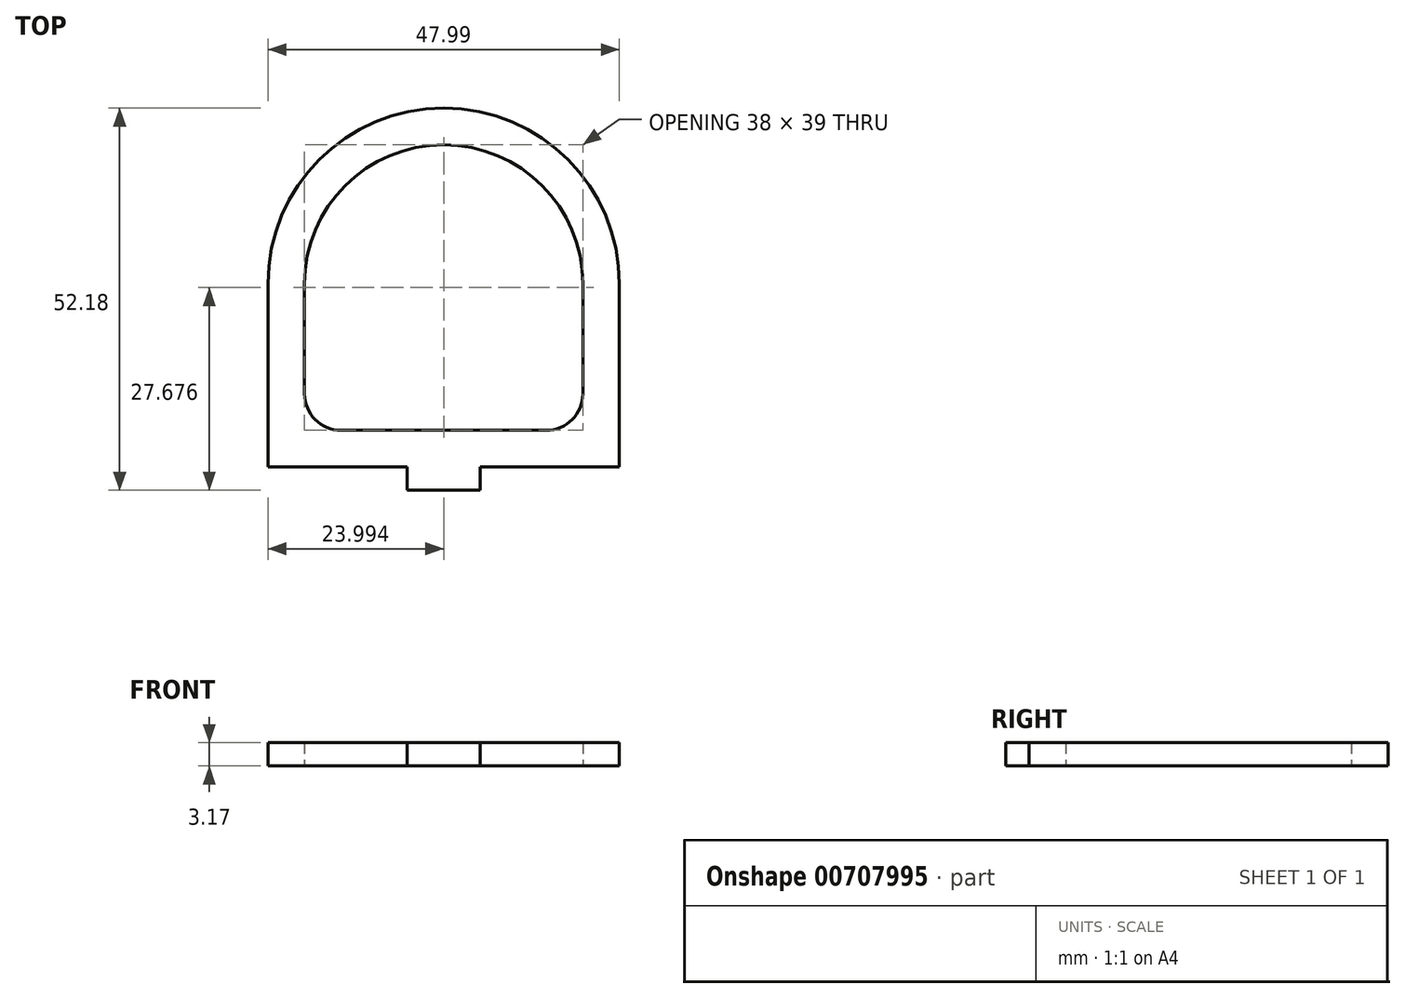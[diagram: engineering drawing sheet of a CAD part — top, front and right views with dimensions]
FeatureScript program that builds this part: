
annotation { "Feature Type Name" : "Feature", "Feature Type Description" : "" }
export const myFeature = defineFeature(function(context is Context, id is Id, definition is map)
    precondition{}
    {
        {
            var Q0;
            Q0=qCreatedBy(makeId("Top.planeOp"), FACE);
            var sketch = newSketch(context, id + "F0", { "sketchPlane" : qUnion([Q0])});
            skPoint(sketch, "E0.0", {"position": v(-25.74, -7.58) * mm});
            skPoint(sketch, "E1.0", {"position": v(-6.75, -7.58) * mm});
            skPoint(sketch, "E2.0", {"position": v(3.25, -7.58) * mm});
            skPoint(sketch, "E3.0", {"position": v(22.25, -7.58) * mm});
            skLineSegment(sketch, "E4", {"start": v(-25.74, -7.58) * mm, "end": v(-6.75, -7.58) * mm});
            skLineSegment(sketch, "E5", {"start": v(-6.75, -7.58) * mm, "end": v(-6.75, -10.76) * mm});
            skLineSegment(sketch, "E6", {"start": v(-6.75, -10.76) * mm, "end": v(3.25, -10.76) * mm});
            skLineSegment(sketch, "E7", {"start": v(3.25, -10.76) * mm, "end": v(3.25, -7.58) * mm});
            skLineSegment(sketch, "E8", {"start": v(3.25, -7.58) * mm, "end": v(22.25, -7.58) * mm});
            skLineSegment(sketch, "E9", {"start": v(-25.74, -7.58) * mm, "end": v(-25.74, 17.42) * mm});
            skLineSegment(sketch, "E10", {"start": v(22.25, 17.42) * mm, "end": v(22.25, -7.58) * mm});
            skArc(sketch, "E11", {"start": v(22.25, 17.42) * mm, "mid": v(-1.75, 41.42) * mm, "end": v(-25.74, 17.42) * mm});
            skArc(sketch, "E12.0", {"start": v(17.25, 17.42) * mm, "mid": v(-1.75, 36.42) * mm, "end": v(-20.74, 17.42) * mm});
            skLineSegment(sketch, "E13.0", {"start": v(17.25, 12.42) * mm, "end": v(17.25, 2.42) * mm});
            skLineSegment(sketch, "E13.1", {"start": v(3.25, -2.58) * mm, "end": v(12.25, -2.58) * mm});
            skLineSegment(sketch, "E14.0", {"start": v(-15.74, -2.58) * mm, "end": v(-6.75, -2.58) * mm});
            skLineSegment(sketch, "E14.1", {"start": v(-20.74, 2.42) * mm, "end": v(-20.74, 12.42) * mm});
            skLineSegment(sketch, "E15", {"start": v(-6.75, -2.58) * mm, "end": v(3.25, -2.58) * mm});
            skPoint(sketch, "E16.visualSharp", {"position": v(-20.74, -2.58) * mm});
            skArc(sketch, "E16.filletArc", {"start": v(-20.74, 2.42) * mm, "mid": v(-19.28, -1.12) * mm, "end": v(-15.74, -2.58) * mm});
            skPoint(sketch, "E17.visualSharp", {"position": v(17.25, -2.58) * mm});
            skArc(sketch, "E17.filletArc", {"start": v(12.25, -2.58) * mm, "mid": v(15.79, -1.12) * mm, "end": v(17.25, 2.42) * mm});
            skLineSegment(sketch, "E18", {"start": v(-20.74, 17.42) * mm, "end": v(-20.74, 12.42) * mm});
            skLineSegment(sketch, "E19", {"start": v(17.25, 17.42) * mm, "end": v(17.25, 12.42) * mm});
            skSolve(sketch);
        }
        {
            var Q0;
            Q0 = qSketchRegion(id + "F0", true);
            extrude(context, id + "F1", {"entities" : qUnion([Q0]), "depth" : 3.17 * mm, "offsetDistance" : 25 * mm});
        }
    });
